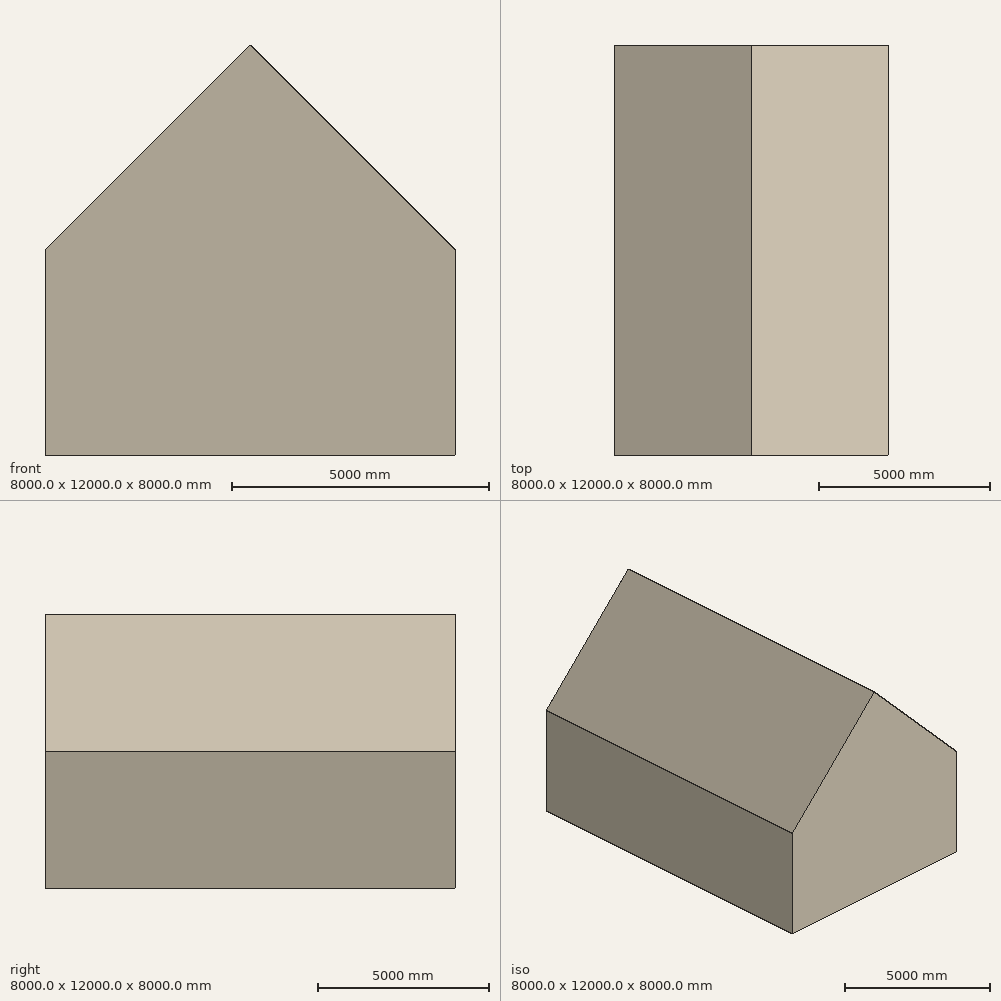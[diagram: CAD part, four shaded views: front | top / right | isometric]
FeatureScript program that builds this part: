
annotation { "Feature Type Name" : "Feature", "Feature Type Description" : "" }
export const myFeature = defineFeature(function(context is Context, id is Id, definition is map)
    precondition{}
    {
        {
            var Q0;
            Q0=qCreatedBy(makeId("Front.planeOp"),FACE);
            var sketch = newSketch(context, id + "F0", { "sketchPlane" : qUnion([Q0])});
            skLineSegment(sketch, "E0.bottom", {"start": v(0, 0) * mm, "end": v(-8000, 0) * mm});
            skLineSegment(sketch, "E0.top", {"start": v(0, 4000) * mm, "end": v(-8000, 4000) * mm});
            skLineSegment(sketch, "E0.left", {"start": v(0, 0) * mm, "end": v(0, 4000) * mm});
            skLineSegment(sketch, "E0.right", {"start": v(-8000, 0) * mm, "end": v(-8000, 4000) * mm});
            skLineSegment(sketch, "E1", {"start": v(-4000, 0) * mm, "end": v(-4000, 8000) * mm});
            skPoint(sketch, "E1.endSnap0", {"position": v(-4000, 0) * mm});
            skLineSegment(sketch, "E2", {"start": v(-4000, 8000) * mm, "end": v(-8000, 4000) * mm});
            skLineSegment(sketch, "E3", {"start": v(-4000, 8000) * mm, "end": v(0, 4000) * mm});
            skSolve(sketch);
        }
        {
            var Q0;
            Q0 = qSketchRegion(id + "F0", true);
            extrude(context, id + "F1", {"entities" : qUnion([Q0]), "depth" : 12000 * mm});
        }
    });
